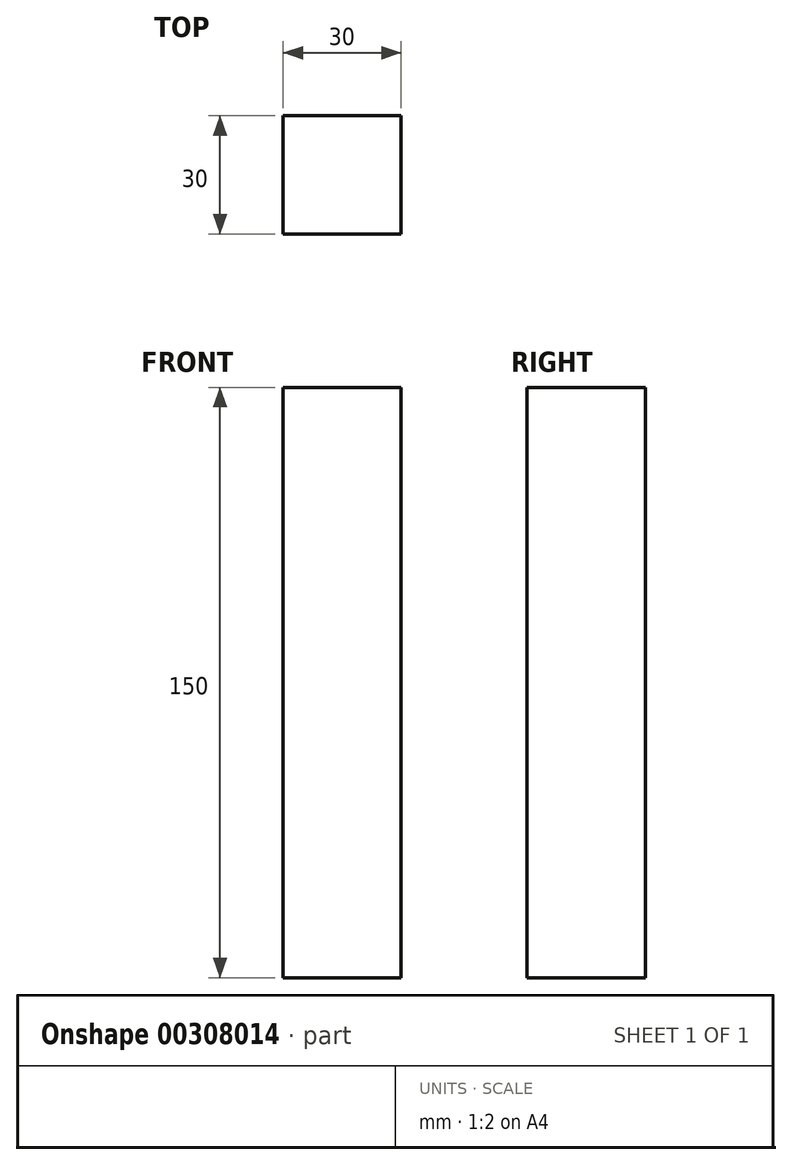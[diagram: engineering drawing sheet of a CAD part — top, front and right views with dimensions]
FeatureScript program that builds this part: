
annotation { "Feature Type Name" : "Feature", "Feature Type Description" : "" }
export const myFeature = defineFeature(function(context is Context, id is Id, definition is map)
    precondition{}
    {
        {
            var Q0;
            Q0=qCreatedBy(makeId("Top.planeOp"),FACE);
            var sketch = newSketch(context, id + "F0", { "sketchPlane" : qUnion([Q0])});
            skLineSegment(sketch, "E0.bottom", {"start": v(15, 15) * mm, "end": v(-15, 15) * mm});
            skLineSegment(sketch, "E0.top", {"start": v(15, -15) * mm, "end": v(-15, -15) * mm});
            skLineSegment(sketch, "E0.left", {"start": v(15, 15) * mm, "end": v(15, -15) * mm});
            skLineSegment(sketch, "E0.right", {"start": v(-15, 15) * mm, "end": v(-15, -15) * mm});
            skPoint(sketch, "E0.middle", {"position": v(0, 0) * mm});
            skSolve(sketch);
        }
        {
            var Q0;
            Q0 = qSketchRegion(id + "F0", true);
            extrude(context, id + "F1", {"entities" : qUnion([Q0]), "endBound" : BoundingType.SYMMETRIC, "depth" : 150 * mm});
        }
    });
